# Revit family: Franke_A600_MS_EC_FW
name_source: partatom
category: Sonderausstattung
revit_build: Autodesk Revit 2015 (Build: 20140606_1530(x64)
units: mm (PartAtom-declared; Revit-internal decimal feet)

## types (2) — shared parameters
Anzahl der Nullleiter (A600) = 1
Anzahl der Schutzleiter (A600) = 1
Anzahl von Polen (A600) = 1
Aufstellgewicht = 38 kg
Bauelement = Kaffeevollautomat
Baugruppenkennzeichen = Kaffeevollautomat
Beschreibung = Mikroprozessorgesteuerter Kaffeevollautomat mit 2 Präzisionskaffeemühlen
Breite = 340 mm  [stored 1.11549 ft]
Durchmesser Abwasser = 9 mm  [stored 0.0295276 ft]
Durchmesser Zuwasser = 8 mm  [stored 0.0262467 ft]
Energieverlust nach DIN18873(A600) = 1.604 kWh/24 h - 230 V
Hersteller = Franke
Höhe = 796 mm  [stored 2.61155 ft]
Leistung max. (A600) = 2800 W
Leistung min. (A600) = 2400 W
Modell = 410915 - A600 MS EC FW
Netzfrequenz (A600) = 50 Hz
Netzfrequenz alternativ (A600) = 60 Hz
Schallemission = 70 dB
Sicherung (A600) = 16 A
Spannung max. (A600) = 240 V
Spannung min. (A600) = 220 V
Tiefe = 600 mm
URL = http://www.franke.com
Wasserdruck = 800000.0 Pa
Wasserdruck (mit Wasserfilter) = 600000.0 Pa
zero-valued in all types: Kosten

## per-type parameters (varying)
| type | Abdeckung Front |
| A600 MS EC FW(220-240V/black line/EU) | Franke Black |
| A600 MS EC FW(220-240V/anthrazit/EU) | Franke Anthrazit |

note: [stored X ft] marks values corroborated as IEEE doubles in the binary element streams (Revit-internal decimal feet)
